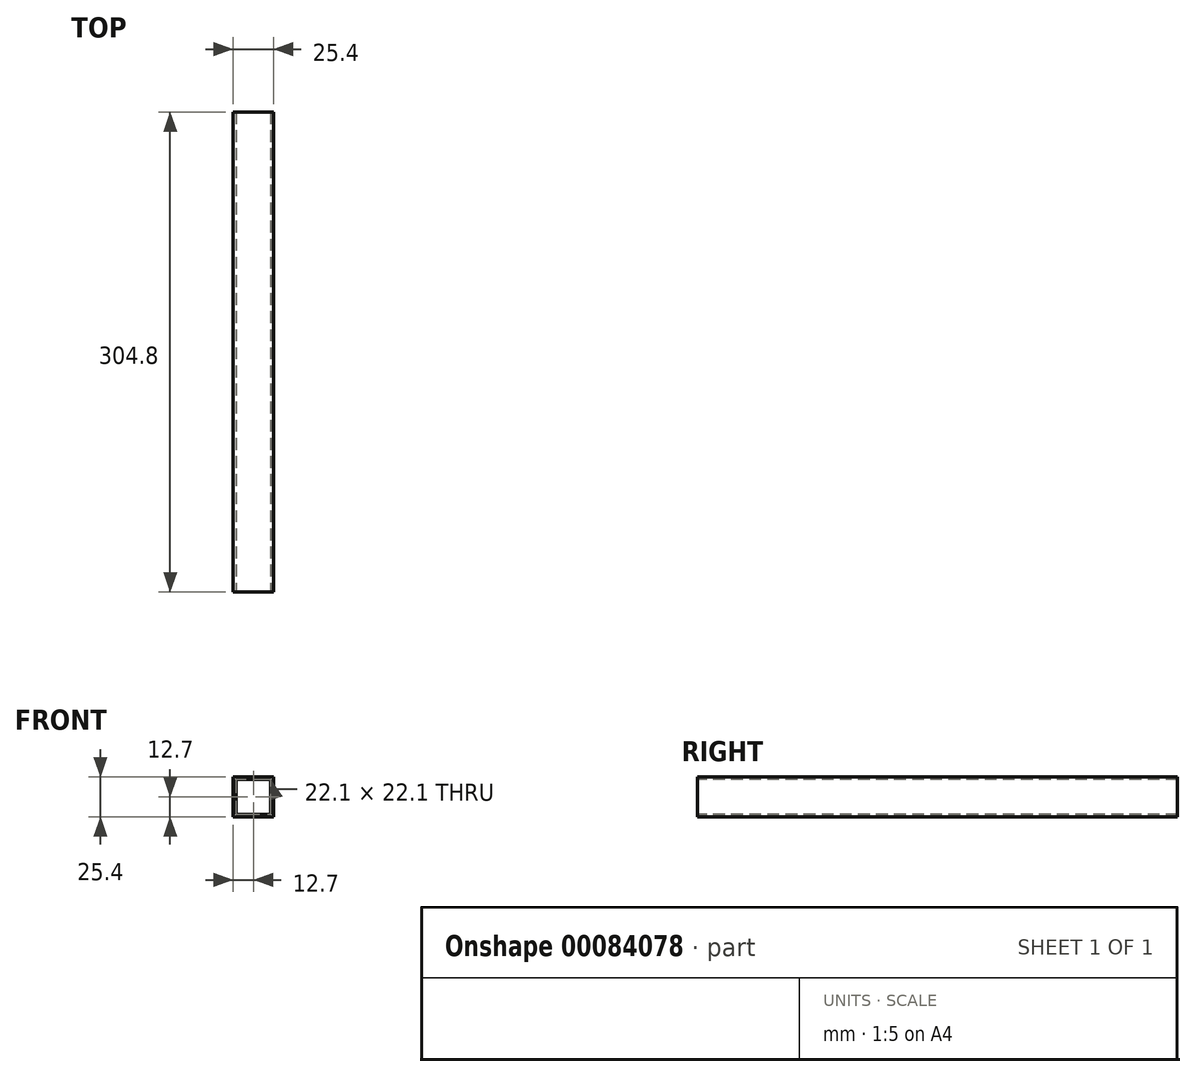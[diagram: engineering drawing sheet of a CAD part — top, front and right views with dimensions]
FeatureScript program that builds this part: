
annotation { "Feature Type Name" : "Feature", "Feature Type Description" : "" }
export const myFeature = defineFeature(function(context is Context, id is Id, definition is map)
    precondition{}
    {
        {
            var Q0;
            Q0=qCreatedBy(makeId("Front.planeOp"),FACE);
            var sketch = newSketch(context, id + "F0", { "sketchPlane" : qUnion([Q0])});
            skLineSegment(sketch, "E0.rect.bottom", {"start": v(12.7, -12.7) * mm, "end": v(-12.7, -12.7) * mm});
            skLineSegment(sketch, "E0.rect.top", {"start": v(12.7, 12.7) * mm, "end": v(-12.7, 12.7) * mm});
            skLineSegment(sketch, "E0.rect.left", {"start": v(12.7, -12.7) * mm, "end": v(12.7, 12.7) * mm});
            skLineSegment(sketch, "E0.rect.right", {"start": v(-12.7, -12.7) * mm, "end": v(-12.7, 12.7) * mm});
            skPoint(sketch, "E0.rect.middle", {"position": v(0, 0) * mm});
            skLineSegment(sketch, "E1.rect.bottom", {"start": v(11.05, -11.05) * mm, "end": v(-11.05, -11.05) * mm});
            skLineSegment(sketch, "E1.rect.top", {"start": v(11.05, 11.05) * mm, "end": v(-11.05, 11.05) * mm});
            skLineSegment(sketch, "E1.rect.left", {"start": v(11.05, -11.05) * mm, "end": v(11.05, 11.05) * mm});
            skLineSegment(sketch, "E1.rect.right", {"start": v(-11.05, -11.05) * mm, "end": v(-11.05, 11.05) * mm});
            skSolve(sketch);
        }
        {
            var Q0;
            Q0=qSketchRegion(id+"F0",true);
            extrude(context, id + "F1", {"entities" : qUnion([Q0]), "oppositeDirection" : true, "depth" : 304.8 * mm});
        }
    });
